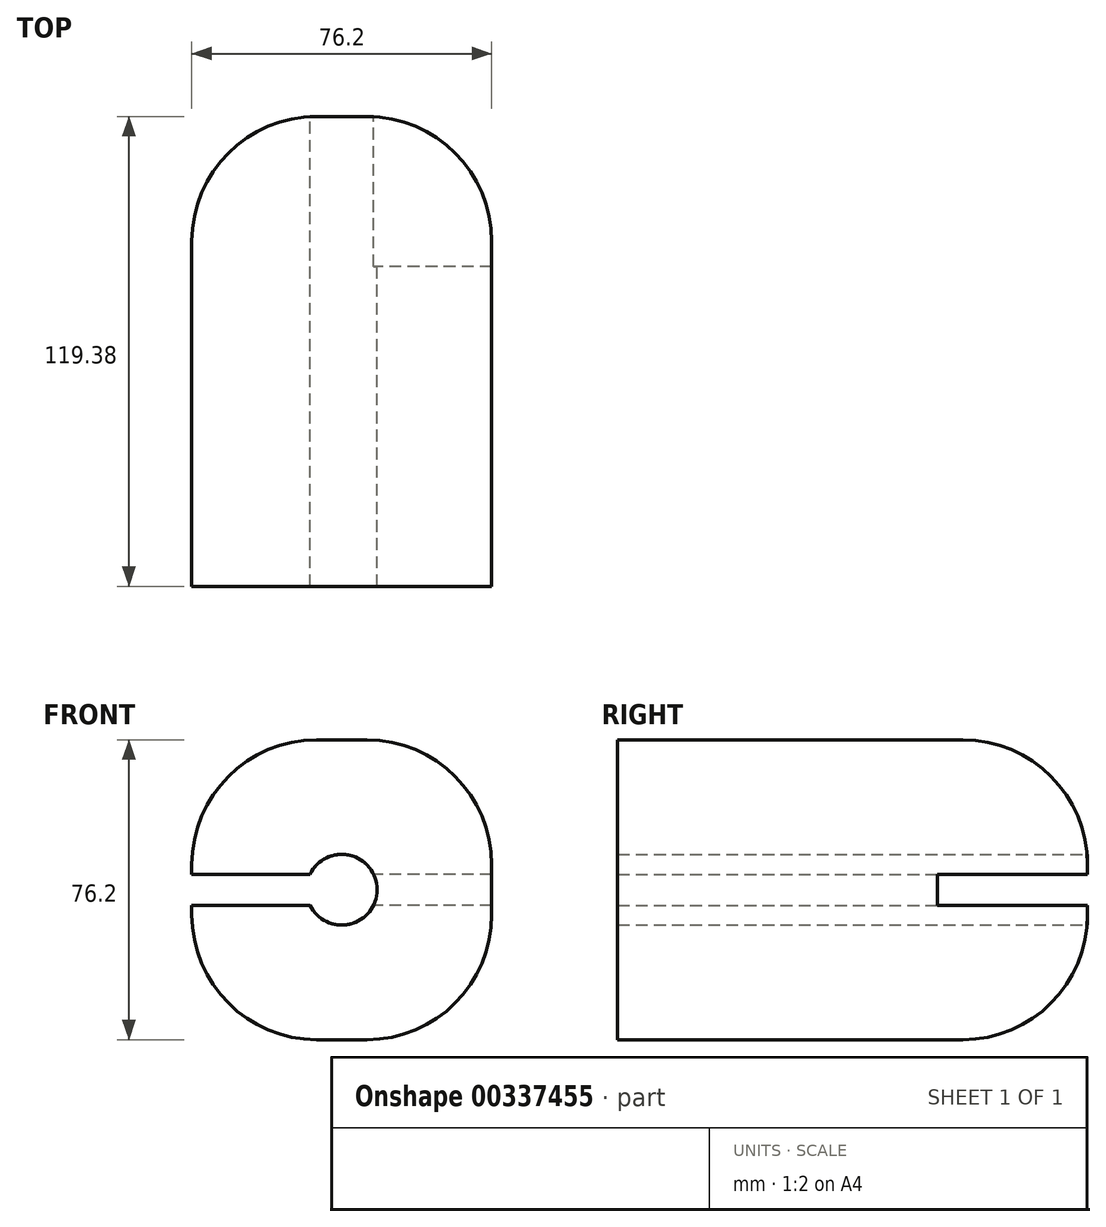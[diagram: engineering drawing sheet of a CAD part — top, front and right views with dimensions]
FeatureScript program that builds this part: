
annotation { "Feature Type Name" : "Feature", "Feature Type Description" : "" }
export const myFeature = defineFeature(function(context is Context, id is Id, definition is map)
    precondition{}
    {
        {
            var Q0;
            Q0=qCreatedBy(makeId("Front.planeOp"),FACE);
            var sketch = newSketch(context, id + "F0", { "sketchPlane" : qUnion([Q0])});
            skLineSegment(sketch, "E0.bottom", {"start": v(-38.1, 38.1) * mm, "end": v(38.1, 38.1) * mm});
            skLineSegment(sketch, "E0.top", {"start": v(-38.1, -38.1) * mm, "end": v(38.1, -38.1) * mm});
            skLineSegment(sketch, "E0.left", {"start": v(-38.1, 38.1) * mm, "end": v(-38.1, -38.1) * mm});
            skLineSegment(sketch, "E0.right", {"start": v(38.1, 38.1) * mm, "end": v(38.1, -38.1) * mm});
            skPoint(sketch, "E0.middle", {"position": v(0, 0) * mm});
            skLineSegment(sketch, "E1.bottom", {"start": v(-38.1, 3.93) * mm, "end": v(38.1, 3.93) * mm});
            skLineSegment(sketch, "E1.top", {"start": v(-38.1, -3.93) * mm, "end": v(38.1, -3.93) * mm});
            skLineSegment(sketch, "E1.left", {"start": v(-38.1, 3.93) * mm, "end": v(-38.1, -3.93) * mm});
            skLineSegment(sketch, "E1.right", {"start": v(38.1, 3.93) * mm, "end": v(38.1, -3.93) * mm});
            skCircle(sketch, "E2", {"center": v(0, 0) * mm, "radius": 8.98 * mm});
            skSolve(sketch);
        }
        {
            var Q0;
            {var subQ0=sQuery(id+"F0.wireOp",EDGE,"E2");var subQ1=sQuery(id+"F0.wireOp",EDGE,"E1.bottom");var subQ2=makeQuery(id+"F0.imprint","INTERSECT",VERTEX,{"disambiguationData":[OD(0.0)],"derivedFrom":[subQ1,subQ0]});Q0=makeQuery(id+"F0.imprint","IMPRINT",FACE,{"disambiguationData":[TD([[makeQuery(id+"F0.imprint","IMPRINT",EDGE,{"disambiguationData":[TD([[subQ2,-1.0]])],"derivedFrom":subQ1}),1.0]])]});}
            var Q1;
            {var subQ0=sQuery(id+"F0.wireOp",EDGE,"E2");var subQ1=sQuery(id+"F0.wireOp",EDGE,"E1.top");var subQ2=makeQuery(id+"F0.imprint","INTERSECT",VERTEX,{"disambiguationData":[OD(0.0)],"derivedFrom":[subQ1,subQ0]});Q1=makeQuery(id+"F0.imprint","IMPRINT",FACE,{"disambiguationData":[TD([[makeQuery(id+"F0.imprint","IMPRINT",EDGE,{"disambiguationData":[TD([[subQ2,-1.0]])],"derivedFrom":subQ1}),-1.0]])]});}
            var Q2;
            {var subQ0=sQuery(id+"F0.wireOp",EDGE,"E2");var subQ1=sQuery(id+"F0.wireOp",EDGE,"E1.bottom");var subQ2=makeQuery(id+"F0.imprint","INTERSECT",VERTEX,{"disambiguationData":[OD(0.0)],"derivedFrom":[subQ1,subQ0]});Q2=makeQuery(id+"F0.imprint","IMPRINT",FACE,{"disambiguationData":[TD([[makeQuery(id+"F0.imprint","IMPRINT",EDGE,{"disambiguationData":[TD([[subQ2,-1.0]])],"derivedFrom":subQ1}),-1.0]])]});}
            extrude(context, id + "F1", {"entities" : qUnion([Q0, Q1, Q2]), "depth" : 81.28 * mm});
        }
        {
            var Q0;
            {var subQ6=sQuery(id+"F0.wireOp",EDGE,"E0.bottom");Q0=makeQuery(id+"F0.imprint","IMPRINT",FACE,{"disambiguationData":[TD([[makeQuery(id+"F0.imprint","IMPRINT",EDGE,{"derivedFrom":subQ6}),-1.0]])]});}
            var Q1;
            {var subQ0=sQuery(id+"F0.wireOp",EDGE,"E1.left");Q1=makeQuery(id+"F0.imprint","IMPRINT",FACE,{"disambiguationData":[TD([[makeQuery(id+"F0.imprint","IMPRINT",EDGE,{"derivedFrom":subQ0}),1.0]])]});}
            var Q2;
            {var subQ0=sQuery(id+"F0.wireOp",EDGE,"E1.right");Q2=makeQuery(id+"F0.imprint","IMPRINT",FACE,{"disambiguationData":[TD([[makeQuery(id+"F0.imprint","IMPRINT",EDGE,{"derivedFrom":subQ0}),-1.0]])]});}
            var Q3;
            {var subQ6=sQuery(id+"F0.wireOp",EDGE,"E0.top");Q3=makeQuery(id+"F0.imprint","IMPRINT",FACE,{"disambiguationData":[TD([[makeQuery(id+"F0.imprint","IMPRINT",EDGE,{"derivedFrom":subQ6}),1.0]])]});}
            extrude(context, id + "F2", {"entities" : qUnion([Q0, Q1, Q2, Q3]), "operationType" : NewBodyOperationType.ADD, "endBound" : BoundingType.SYMMETRIC, "depth" : 76.2 * mm});
        }
        {
            var Q0;
            Q0=makeQuery(id+"F2.opExtrude","CAP_EDGE",EDGE,{"disambiguationData":[OSD([sQuery(id+"F0.wireOp",EDGE,"E0.bottom")])],"isStart":false});
            var Q1;
            Q1=makeQuery(id+"F2.opExtrude","CAP_EDGE",EDGE,{"disambiguationData":[OSD([sQuery(id+"F0.wireOp",EDGE,"E0.left"),sQuery(id+"F0.wireOp",EDGE,"E1.left")])],"isStart":false});
            var Q2;
            Q2=makeQuery(id+"F2.opExtrude","CAP_EDGE",EDGE,{"disambiguationData":[OSD([sQuery(id+"F0.wireOp",EDGE,"E0.right"),sQuery(id+"F0.wireOp",EDGE,"E1.right")])],"isStart":false});
            var Q3;
            Q3=makeQuery(id+"F2.opExtrude","CAP_EDGE",EDGE,{"disambiguationData":[OSD([sQuery(id+"F0.wireOp",EDGE,"E0.top")])],"isStart":false});
            var Q4;
            Q4=makeQuery(id+"F2.opExtrude","SWEPT_EDGE",EDGE,{"disambiguationData":[OSD([sQuery(id+"F0.wireOp",EDGE,"E0.top"),sQuery(id+"F0.wireOp",EDGE,"E0.right")])]});
            var Q5;
            Q5=makeQuery(id+"F2.opExtrude","CAP_EDGE",EDGE,{"disambiguationData":[OSD([sQuery(id+"F0.wireOp",EDGE,"E0.right"),sQuery(id+"F0.wireOp",EDGE,"E1.right")])],"isStart":true});
            var Q6;
            Q6=makeQuery(id+"F2.opExtrude","SWEPT_EDGE",EDGE,{"disambiguationData":[OSD([sQuery(id+"F0.wireOp",EDGE,"E0.bottom"),sQuery(id+"F0.wireOp",EDGE,"E0.right")])]});
            var Q7;
            Q7=makeQuery(id+"F2.opExtrude","CAP_EDGE",EDGE,{"disambiguationData":[OSD([sQuery(id+"F0.wireOp",EDGE,"E0.bottom")])],"isStart":true});
            var Q8;
            Q8=makeQuery(id+"F2.opExtrude","CAP_EDGE",EDGE,{"disambiguationData":[OSD([sQuery(id+"F0.wireOp",EDGE,"E0.left"),sQuery(id+"F0.wireOp",EDGE,"E1.left")])],"isStart":true});
            var Q9;
            Q9=makeQuery(id+"F2.opExtrude","CAP_EDGE",EDGE,{"disambiguationData":[OSD([sQuery(id+"F0.wireOp",EDGE,"E0.top")])],"isStart":true});
            var Q10;
            Q10=makeQuery(id+"F2.opExtrude","SWEPT_EDGE",EDGE,{"disambiguationData":[OSD([sQuery(id+"F0.wireOp",EDGE,"E0.top"),sQuery(id+"F0.wireOp",EDGE,"E0.left")])]});
            var Q11;
            Q11=makeQuery(id+"F2.opExtrude","SWEPT_EDGE",EDGE,{"disambiguationData":[OSD([sQuery(id+"F0.wireOp",EDGE,"E0.bottom"),sQuery(id+"F0.wireOp",EDGE,"E0.left")])]});
            fillet(context, id + "F3", {"entities" : qUnion([Q0, Q1, Q2, Q3, Q4, Q5, Q6, Q7, Q8, Q9, Q10, Q11]), "radius" : 31.72 * mm, "tangentPropagation" : true, "allowEdgeOverflow" : false});
        }
    });
